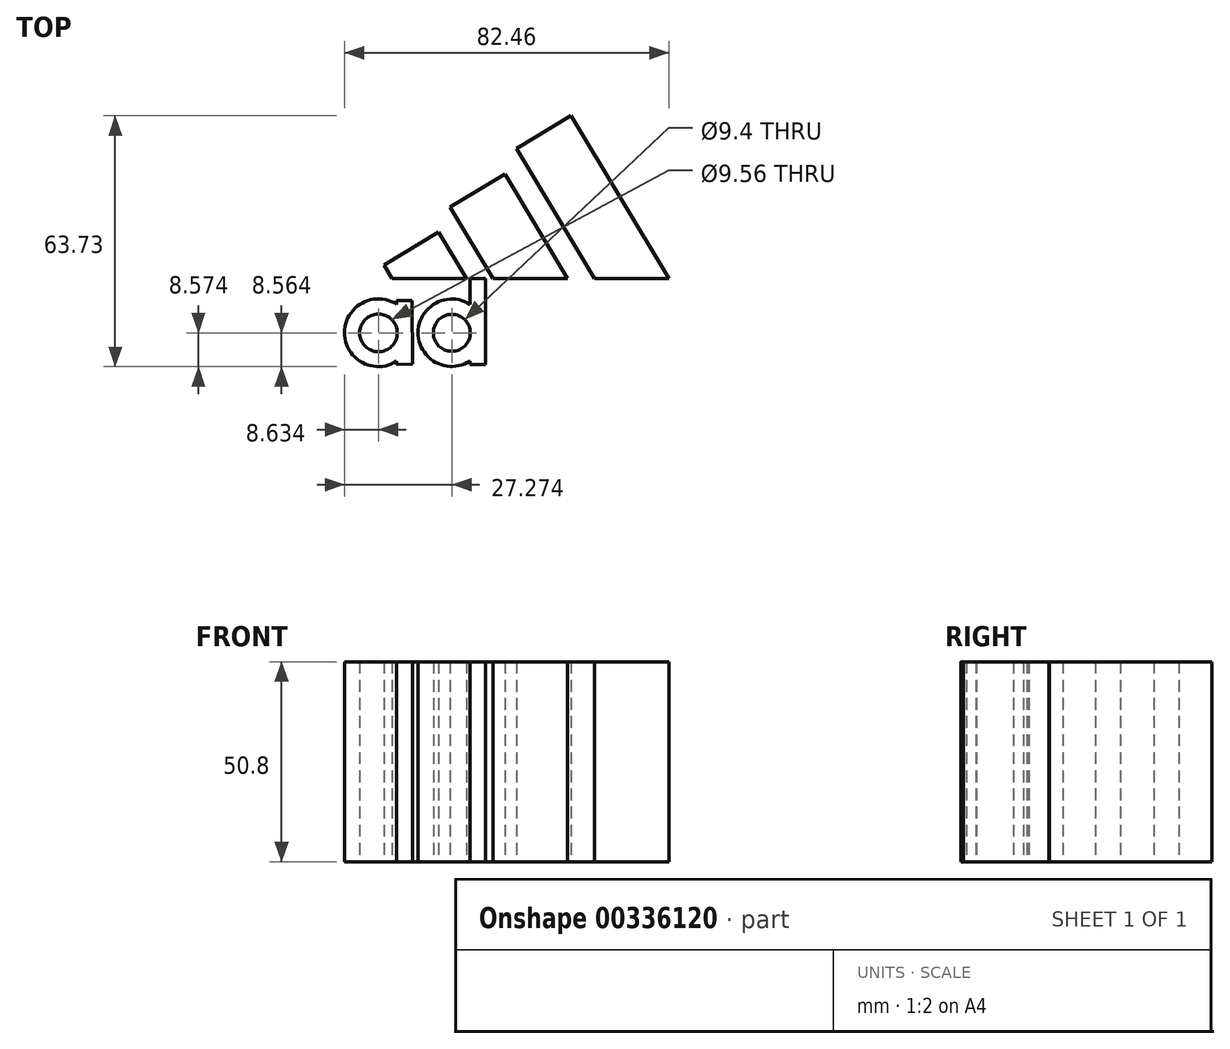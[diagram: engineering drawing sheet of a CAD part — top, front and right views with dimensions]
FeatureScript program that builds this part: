
annotation { "Feature Type Name" : "Feature", "Feature Type Description" : "" }
export const myFeature = defineFeature(function(context is Context, id is Id, definition is map)
    precondition{}
    {
        {
            var Q0;
            Q0=qCreatedBy(makeId("Top.planeOp"),FACE);
            var sketch = newSketch(context, id + "F0", { "sketchPlane" : qUnion([Q0])});
            skLineSegment(sketch, "E0", {"start": v(-38.83, -0.79) * mm, "end": v(-24.9, 7.53) * mm});
            skLineSegment(sketch, "E1", {"start": v(-24.9, 7.53) * mm, "end": v(-17.84, -4.3) * mm});
            skLineSegment(sketch, "E2", {"start": v(-17.84, -4.3) * mm, "end": v(-36.74, -4.3) * mm});
            skLineSegment(sketch, "E3", {"start": v(-36.74, -4.3) * mm, "end": v(-38.83, -0.79) * mm});
            skSolve(sketch);
        }
        {
            var Q0;
            Q0 = qSketchRegion(id + "F0", true);
            extrude(context, id + "F1", {"entities" : qUnion([Q0]), "depth" : 50.8 * mm});
        }
        {
            var Q0;
            Q0=qCreatedBy(makeId("Top.planeOp"),FACE);
            var sketch = newSketch(context, id + "F2", { "sketchPlane" : qUnion([Q0])});
            skLineSegment(sketch, "E4", {"start": v(-21.98, 13.88) * mm, "end": v(-8.08, 22.37) * mm});
            skLineSegment(sketch, "E5", {"start": v(-8.08, 22.37) * mm, "end": v(7.86, -4.18) * mm});
            skLineSegment(sketch, "E6", {"start": v(7.86, -4.18) * mm, "end": v(-11.06, -4.18) * mm});
            skLineSegment(sketch, "E7", {"start": v(-11.06, -4.18) * mm, "end": v(-21.98, 13.88) * mm});
            skSolve(sketch);
        }
        {
            var Q0;
            Q0=makeQuery(id+"F2.imprint","IMPRINT",FACE,{"disambiguationData":[TD([[makeQuery(id+"F2.imprint","IMPRINT",EDGE,{"derivedFrom":sQuery(id+"F2.wireOp",EDGE,"E4")}),-1.0]])]});
            extrude(context, id + "F3", {"entities" : qUnion([Q0]), "depth" : 50.8 * mm});
        }
        {
            var Q0;
            Q0=qCreatedBy(makeId("Top.planeOp"),FACE);
            var sketch = newSketch(context, id + "F4", { "sketchPlane" : qUnion([Q0])});
            skLineSegment(sketch, "E8", {"start": v(-5.13, 28.77) * mm, "end": v(8.7, 37.12) * mm});
            skLineSegment(sketch, "E9", {"start": v(8.7, 37.12) * mm, "end": v(33.64, -4.2) * mm});
            skLineSegment(sketch, "E10", {"start": v(33.64, -4.2) * mm, "end": v(14.64, -4.2) * mm});
            skLineSegment(sketch, "E11", {"start": v(14.64, -4.2) * mm, "end": v(-5.13, 28.77) * mm});
            skSolve(sketch);
        }
        {
            var Q0;
            Q0=makeQuery(id+"F4.imprint","IMPRINT",FACE,{"disambiguationData":[TD([[makeQuery(id+"F4.imprint","IMPRINT",EDGE,{"derivedFrom":sQuery(id+"F4.wireOp",EDGE,"E8")}),-1.0]])]});
            extrude(context, id + "F5", {"entities" : qUnion([Q0]), "depth" : 50.8 * mm});
        }
        {
            var Q0;
            Q0=qCreatedBy(makeId("Top.planeOp"),FACE);
            var sketch = newSketch(context, id + "F6", { "sketchPlane" : qUnion([Q0])});
            skCircle(sketch, "E12", {"center": v(-40.19, -18.05) * mm, "radius": 4.78 * mm});
            skPoint(sketch, "E12.first.point", {"position": v(-40.91, -13.32) * mm});
            skPoint(sketch, "E12.second.point", {"position": v(-39.54, -22.78) * mm});
            skPoint(sketch, "E12.third.point", {"position": v(-44.08, -20.81) * mm});
            skArc(sketch, "E13", {"start": v(-35.53, -10.78) * mm, "mid": v(-48.82, -18) * mm, "end": v(-35.54, -25.23) * mm});
            skLineSegment(sketch, "E14", {"start": v(-35.53, -10.78) * mm, "end": v(-35.53, -9.87) * mm});
            skLineSegment(sketch, "E15", {"start": v(-35.53, -9.87) * mm, "end": v(-31.63, -9.87) * mm});
            skLineSegment(sketch, "E16", {"start": v(-31.63, -9.87) * mm, "end": v(-31.59, -26.02) * mm});
            skLineSegment(sketch, "E17", {"start": v(-31.59, -26.02) * mm, "end": v(-35.53, -26.02) * mm});
            skLineSegment(sketch, "E18", {"start": v(-35.53, -26.02) * mm, "end": v(-35.54, -25.23) * mm});
            skSolve(sketch);
        }
        {
            var Q0;
            Q0 = qSketchRegion(id + "F6", true);
            extrude(context, id + "F7", {"entities" : qUnion([Q0]), "depth" : 50.8 * mm});
        }
        {
            var Q0;
            Q0=qCreatedBy(makeId("Top.planeOp"),FACE);
            var sketch = newSketch(context, id + "F8", { "sketchPlane" : qUnion([Q0])});
            skCircle(sketch, "E19", {"center": v(-21.55, -18.04) * mm, "radius": 4.7 * mm});
            skPoint(sketch, "E19.first.point", {"position": v(-22.45, -13.42) * mm});
            skPoint(sketch, "E19.second.point", {"position": v(-20.64, -22.65) * mm});
            skPoint(sketch, "E19.third.point", {"position": v(-17.21, -19.86) * mm});
            skArc(sketch, "E20", {"start": v(-16.92, -10.82) * mm, "mid": v(-30.13, -17.98) * mm, "end": v(-16.96, -25.21) * mm});
            skLineSegment(sketch, "E21", {"start": v(-16.92, -10.82) * mm, "end": v(-16.92, -4.29) * mm});
            skLineSegment(sketch, "E22", {"start": v(-16.92, -4.29) * mm, "end": v(-12.96, -4.29) * mm});
            skLineSegment(sketch, "E23", {"start": v(-12.96, -4.29) * mm, "end": v(-13.04, -26.06) * mm});
            skLineSegment(sketch, "E24", {"start": v(-13.04, -26.06) * mm, "end": v(-16.92, -26.04) * mm});
            skLineSegment(sketch, "E25", {"start": v(-16.92, -26.04) * mm, "end": v(-16.96, -25.21) * mm});
            skSolve(sketch);
        }
        {
            var Q0;
            Q0 = qSketchRegion(id + "F8", true);
            extrude(context, id + "F9", {"entities" : qUnion([Q0]), "depth" : 50.8 * mm});
        }
    });
